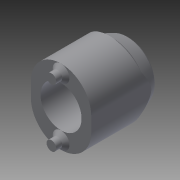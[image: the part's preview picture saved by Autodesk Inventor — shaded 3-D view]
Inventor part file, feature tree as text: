
AUTODESK INVENTOR PART (.ipt)
format: ipt  version: 2014 (Build 180170000, 170)  size: 146,432 bytes
history: native  units: in
note: dims shown in document units (in); Inventor stores cm internally (conversion verified against a paired STEP export)
features: chamfer x4, extrude x3, sketch x3
ambient origin geometry x8: Origin, YZ Plane, XZ Plane, XY Plane, X Axis, Y Axis, Z Axis, Center Point
bodies: Solid1 (feature_tree)
feature tree (10):
  extrude  "Extrusion1"  Depth=0.4921in
  extrude  "Extrusion2"  Depth=0.3937in TaperAngle=0.0deg
  extrude  "Extrusion3"  Depth=0.0787in
  chamfer  "Chamfer1"  Distance=0.0787in
  chamfer  "Chamfer2"  Distance=0.0591in
  chamfer  "Chamfer3"  Distance=0.1575in
  chamfer  "Chamfer4"  Distance=0.0787in Angle=45.0deg
  sketch  "Sketch1"  dims[d0=0.3346in d1=0.4921in]
  sketch  "Sketch2"  dims[d2=0.1181in d3=0.3937in d4=0.0in]
  sketch  "Sketch3"  dims[d5=0.0787in d6=0.2362in d7=0.0787in d8=0.0in d9=0.0591in d10=0.1575in d11=0.0in d12=0.0768in d13=0.0787in d14=45.0deg d15=0.0669in d16=0.0787in d17=45.0deg d18=0.0138in d19=0.0787in d20=45.0deg d21=0.0295in d22=0.0787in d23=45.0deg]
